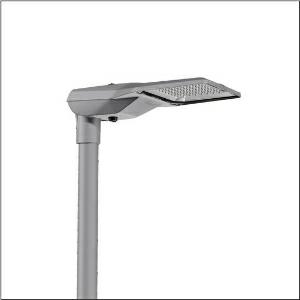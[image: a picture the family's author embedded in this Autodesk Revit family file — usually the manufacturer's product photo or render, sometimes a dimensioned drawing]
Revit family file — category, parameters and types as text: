
# Revit family: streetlight_sl_21_midi___st1_5a_5xe3p33t08mb_b96f
name_source: partatom
category: Lighting Fixtures
units: mm (PartAtom-declared; Revit-internal decimal feet)

## family parameters
Cut with Voids When Loaded = No
Host = Face
Light Source = No
Part Type = Normal
Room Calculation Point = No
Round Connector Dimension = Use Diameter
Shared = No

## types (1)
- --- (1 x LED, 17960 lm, 136 W, 3000K)
    Apparent Load = 136 VA
    CIE Flux Codes = 22 53 95 100 100
    Color Rendering = 70
    Color Temperature = 3000K
    Default Elevation = 1800 mm
    Description = Streetlight SL 21 midi, mast luminaire, primary light control with lens, of PMMA, primary optical cover: cover, of toughened safety glass, transparent, light distribution: ST1.5a, light emission: direct distribution, primary light characteristic: asymmetric, installation type: side-entry, post-top, LED, High Power LED, rated luminous flux: 17.960lm, luminous efficacy: 132lm/W, light colour: 730, colour temperature: 3000K, control gear: D4i, control: overheat protection, constant luminous flux control, time-dependent luminous flux control, flexible luminous flux parameterisation, pre-setting: logarithmic dimming characteristic, mains connection: 230..240V, AC, 50/60Hz, start of lifetime: 136W, end of service life: 142W, reduction: 61W, luminaire housing, of diecast aluminium, powder-coated, Siteco® metallic grey (DB 702S), corrosivity category C5 mid according to DIN EN ISO 12944, please order mast flange separately, inclination adjustable: 0°, 5°, 10°, 15°, sealing non-destructively replaceable, multi-level sealing system, length: 644mm, width: 335mm, height: 110mm, mast flange for spigot size: 42mm (side-entry): 5XC10008XM4, 60/48mm (side-entry/post-top): 5XC10108XM2, 76/60mm (side-entry/post-top): 5XC10108XM1, mounting height: 4..8m, Smart Interface below and above, protection rating (complete): IP66, insulation class (complete): insulation class II (safety insulation), certification: CE, ENEC, ENEC+, VDE, impact resistance: IK10, permissible operating ambient temperature for outdoor applications: -40..+50°C, standard-compliant lighting for roads and squares, packaging unit: 1 piece

Light Distribution: ST1.5a
    Height = 111 mm
    Lamp = 1 x LED
    Lamp Light Flux = 17960 lm
    Lamp Power = 136 W
    Lamp count = 1
    Length = 644 mm
    Luminous efficacy = 132 lm/W
    Manufacturer = Siteco
    ModVariant = No
    Model = 5XE3P33T08MB
    Number of Poles = 1
    OnlyDefault = Yes
    Power Factor = 1
    Product Name = Streetlight SL 21 midi | ST1.5a
    Product group = mast luminaire | pylon top
    ProductGroupID = 6100
    Protection Class = Protection class II
    Protection Degree = IP 66
    RLX_Detail_Level = 1
    RLX_Emergency_Light_Flux = 0 lm
    RLX_Emergency_Type = 0
    RLX_Emergency_Type_DB = No
    RlxData = <blob elided: 30573 chars, md5=88de0523>
    Socket = socket
    Standby Power = 0 W
    System Light Flux = 17960 lm
    System Power = 136 W
    Type Comments = factory setting: luminous flux: 100 % | dim-lin: 254 | 695 mA
    Type Image = l_1004304.jpg
    URL = http://relux.com
    VarID = @adj_197571
    Voltage = 0 V
    Weight = 0.00 kg
    Width = 336 mm

## geometry (parser evidence)
native form markers: Blend x4, Sweep x11
no freeform markers — native parametric forms only
